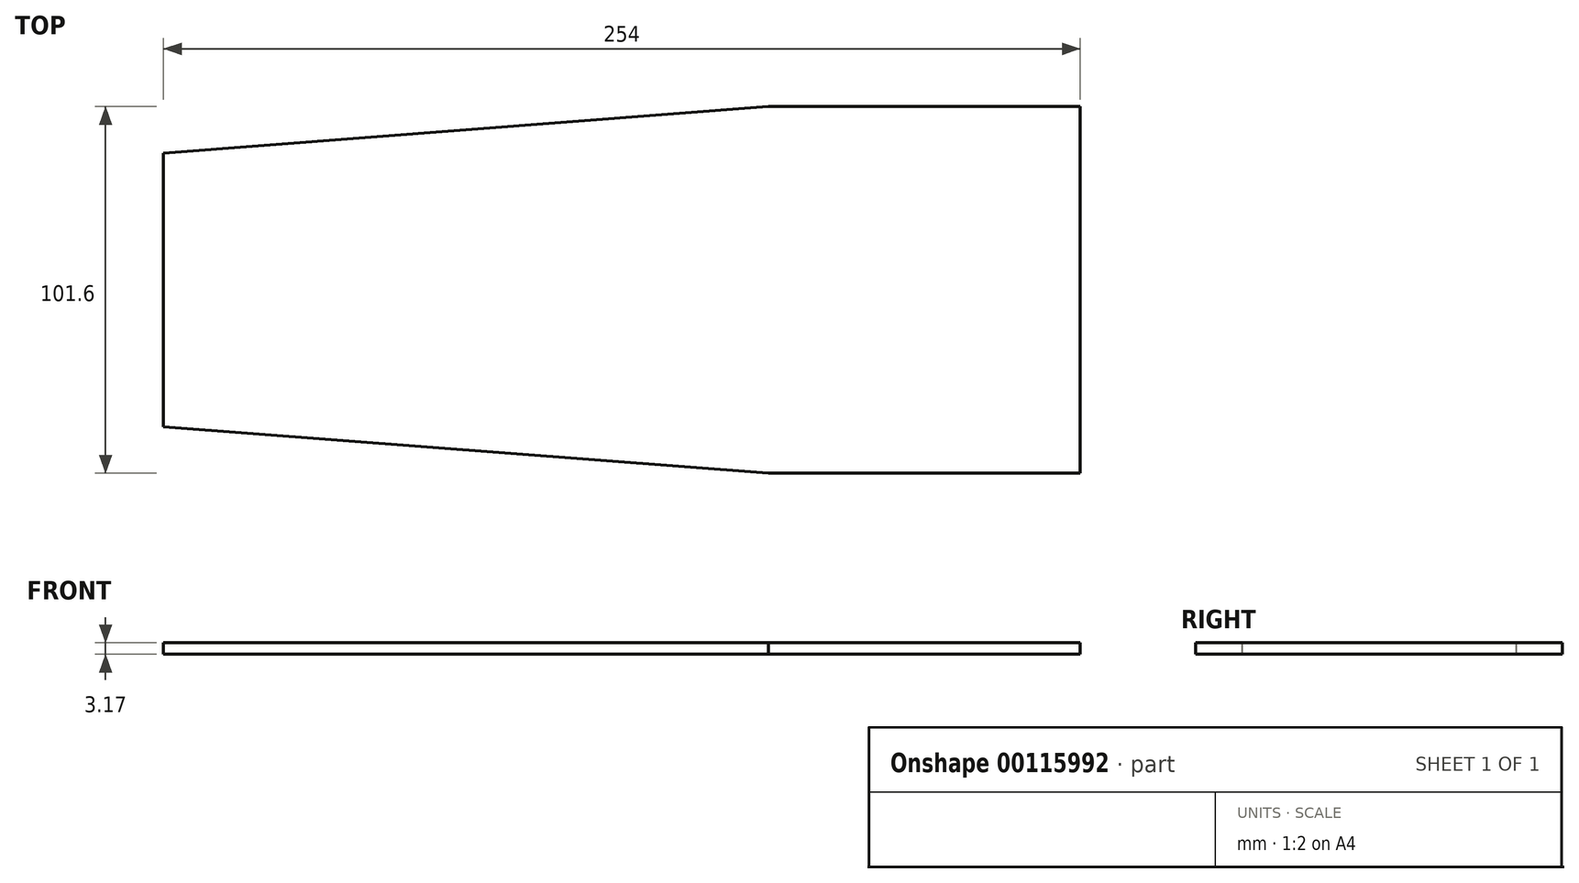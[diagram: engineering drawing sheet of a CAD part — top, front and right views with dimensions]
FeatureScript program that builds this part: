
annotation { "Feature Type Name" : "Feature", "Feature Type Description" : "" }
export const myFeature = defineFeature(function(context is Context, id is Id, definition is map)
    precondition{}
    {
        {
            var Q0;
            Q0=qCreatedBy(makeId("Top.planeOp"),FACE);
            var sketch = newSketch(context, id + "F0", { "sketchPlane" : qUnion([Q0])});
            skLineSegment(sketch, "E0", {"start": v(23.17, 50.8) * mm, "end": v(-144.38, 37.95) * mm});
            skLineSegment(sketch, "E1.MirrorCS", {"start": v(23.17, -50.8) * mm, "end": v(-144.38, -37.95) * mm});
            skLineSegment(sketch, "E2.bottom", {"start": v(23.17, 50.8) * mm, "end": v(109.62, 50.8) * mm});
            skLineSegment(sketch, "E2.top", {"start": v(23.17, -50.8) * mm, "end": v(109.62, -50.8) * mm});
            skLineSegment(sketch, "E2.right", {"start": v(109.62, 50.8) * mm, "end": v(109.62, -50.8) * mm});
            skLineSegment(sketch, "E3", {"start": v(-144.38, 37.95) * mm, "end": v(-144.38, -37.95) * mm});
            skSolve(sketch);
        }
        {
            var Q0;
            Q0=makeQuery(id+"F0.imprint","IMPRINT",FACE,{"disambiguationData":[TD([[makeQuery(id+"F0.imprint","IMPRINT",EDGE,{"derivedFrom":sQuery(id+"F0.wireOp",EDGE,"E0")}),1.0]])]});
            extrude(context, id + "F1", {"entities" : qUnion([Q0]), "depth" : 3.17 * mm});
        }
    });
